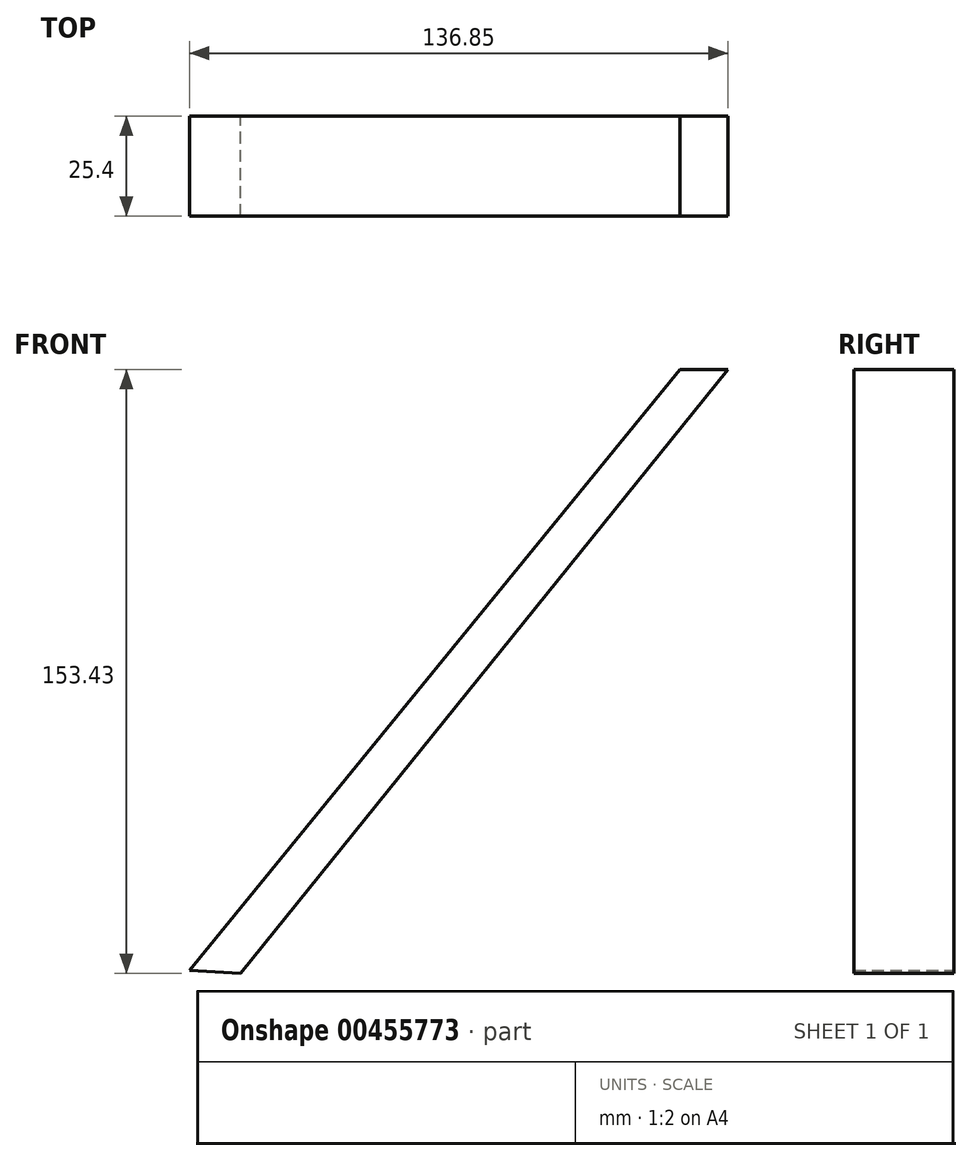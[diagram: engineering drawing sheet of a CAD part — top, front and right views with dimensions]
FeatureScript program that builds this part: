
annotation { "Feature Type Name" : "Feature", "Feature Type Description" : "" }
export const myFeature = defineFeature(function(context is Context, id is Id, definition is map)
    precondition{}
    {
        {
            var Q0;
            Q0=qCreatedBy(makeId("Front.planeOp"),FACE);
            var sketch = newSketch(context, id + "F0", { "sketchPlane" : qUnion([Q0])});
            skLineSegment(sketch, "E0", {"start": v(-76.1, -76.1) * mm, "end": v(48.54, 76.6) * mm});
            skLineSegment(sketch, "E1", {"start": v(48.54, 76.6) * mm, "end": v(60.74, 76.6) * mm});
            skLineSegment(sketch, "E2", {"start": v(60.74, 76.6) * mm, "end": v(-63.18, -76.84) * mm});
            skLineSegment(sketch, "E3", {"start": v(-63.18, -76.84) * mm, "end": v(-76.1, -76.1) * mm});
            skSolve(sketch);
        }
        {
            var Q0;
            Q0 = qSketchRegion(id + "F0", true);
            extrude(context, id + "F1", {"entities" : qUnion([Q0]), "depth" : 25.4 * mm});
        }
    });
